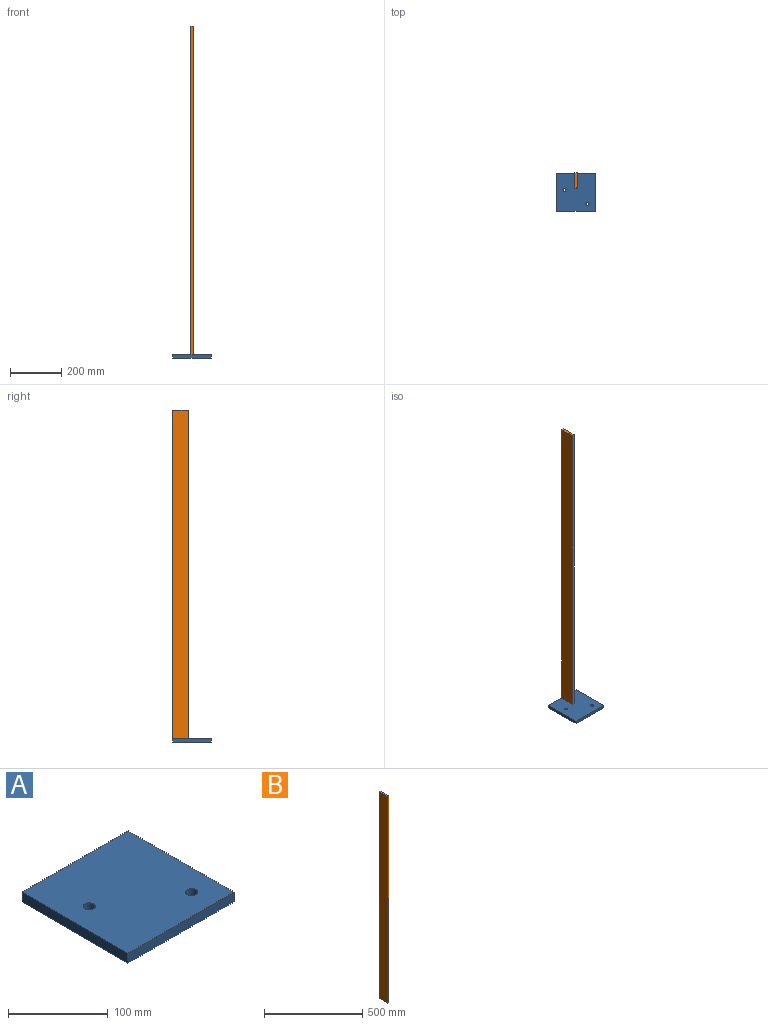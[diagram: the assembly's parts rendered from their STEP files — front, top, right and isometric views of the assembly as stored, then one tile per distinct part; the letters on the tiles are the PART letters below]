
ASSEMBLY  parts=2 mates=1
PART A: 8 faces, bbox 150x150x12 mm
  f0: plane 150x12mm, normal (1,0,0), area 1800mm2, adj f1,f3,f4,f5
  f1: plane 150x12mm, normal (0,1,0), area 1800mm2, adj f0,f2,f4,f5
  f2: plane 150x12mm, normal (-1,0,0), area 1800mm2, adj f1,f3,f4,f5
  f3: plane 150x12mm, normal (0,-1,0), area 1800mm2, adj f0,f2,f4,f5
  f4: plane 150x150mm, normal (0,0,1), area 22273.8mm2, adj f0,f1,f2,f3,f6,f7
  f5: plane 150x150mm, normal (0,0,-1), area 22273.8mm2, adj f0,f1,f2,f3,f6,f7
  f6: cylinder r=6mm len=12mm, axis (0,0,1), area 452.4mm2, adj f4,f5
  f7: cylinder r=6mm len=12mm, axis (0,0,1), area 452.4mm2, adj f4,f5
PART B: 6 faces, bbox 10x60x1288 mm
  f0: plane 1288x60mm, normal (-1,0,0), area 77280mm2, adj f1,f3,f4,f5
  f1: plane 1288x10mm, normal (0,-1,0), area 12880mm2, adj f0,f2,f4,f5
  f2: plane 1288x60mm, normal (1,0,0), area 77280mm2, adj f1,f3,f4,f5
  f3: plane 1288x10mm, normal (0,1,0), area 12880mm2, adj f0,f2,f4,f5
  f4: plane 60x10mm, normal (0,0,1), area 600mm2, adj f0,f1,f2,f3
  f5: plane 60x10mm, normal (0,0,-1), area 600mm2, adj f0,f1,f2,f3
PLACE A t=(-182.71,74.55,-454.49)mm
PLACE B t=(-187.71,89.73,-442.49)mm
MATE fastened A.f4 <-> B.f5  axis (0,0,1) through (-182.71,119.73,-442.49)mm
